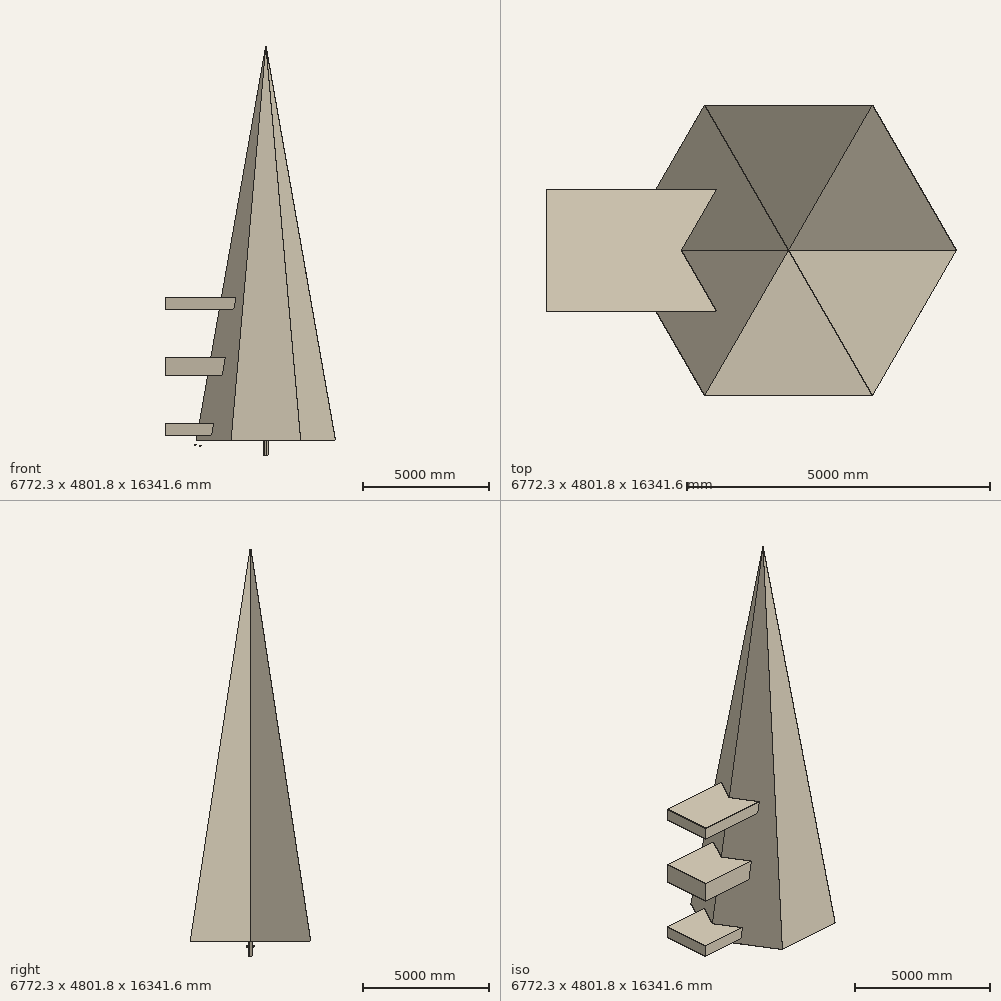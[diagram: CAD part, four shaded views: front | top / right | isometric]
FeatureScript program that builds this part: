
annotation { "Feature Type Name" : "Feature", "Feature Type Description" : "" }
export const myFeature = defineFeature(function(context is Context, id is Id, definition is map)
    precondition{}
    {
        {
            var Q0;
            Q0=qCreatedBy(makeId("Front.planeOp"),FACE);
            var sketch = newSketch(context, id + "F0", { "sketchPlane" : qUnion([Q0])});
            skLineSegment(sketch, "E0", {"start": v(-4000, 0) * mm, "end": v(4000, 0) * mm, "construction": true});
            skLineSegment(sketch, "E1", {"start": v(0, 7000) * mm, "end": v(0, -7000) * mm, "construction": true});
            skSolve(sketch);
        }
        {
            var Q0;
            Q0=qCreatedBy(makeId("Front.planeOp"),FACE);
            var sketch = newSketch(context, id + "F1", { "sketchPlane" : qUnion([Q0])});
            skLineSegment(sketch, "E2", {"start": v(0, 0) * mm, "end": v(0, 1682.58) * mm});
            skLineSegment(sketch, "E3.0", {"start": v(-2535.84, 600) * mm, "end": v(-2535.84, 612.7) * mm});
            skLineSegment(sketch, "E4", {"start": v(-3676.33, 0) * mm, "end": v(-2212.14, 0) * mm, "construction": true});
            skLineSegment(sketch, "E5.0", {"start": v(-2942.24, 600) * mm, "end": v(-2535.84, 600) * mm});
            skLineSegment(sketch, "E6.0", {"start": v(-2942.24, 612.7) * mm, "end": v(-2535.84, 612.7) * mm});
            skLineSegment(sketch, "E7.0", {"start": v(-2942.24, 600) * mm, "end": v(-2942.24, 612.7) * mm});
            skPoint(sketch, "E8.orphan", {"position": v(-2535.84, 0) * mm});
            skSolve(sketch);
        }
        {
            var Q0;
            Q0=makeQuery(id+"F1.imprint","IMPRINT",FACE,{"disambiguationData":[TD([[makeQuery(id+"F1.imprint","IMPRINT",EDGE,{"derivedFrom":sQuery(id+"F1.wireOp",EDGE,"E3.0")}),1.0]])]});
            extrude(context, id + "F2", {"entities" : qUnion([Q0]), "depth" : 304.8 * mm, "offsetDistance" : 25 * mm, "symmetric" : true});
        }
        {
            var Q0;
            Q0=makeQuery(id+"F2.opExtrude","CAP_FACE",FACE,{"disambiguationData":[OSD([sQuery(id+"F1.wireOp",EDGE,"E3.0"),sQuery(id+"F1.wireOp",EDGE,"E5.0"),sQuery(id+"F1.wireOp",EDGE,"E6.0"),sQuery(id+"F1.wireOp",EDGE,"E7.0")])],"isStart":false});
            var sketch = newSketch(context, id + "F3", { "sketchPlane" : qUnion([Q0])});
            skPoint(sketch, "E9.0", {"position": v(-2942.24, 606.35) * mm});
            skPoint(sketch, "E10.0", {"position": v(-2535.84, 606.35) * mm});
            skLineSegment(sketch, "E11", {"start": v(-2942.24, 606.35) * mm, "end": v(-2535.84, 606.35) * mm, "construction": true});
            skLineSegment(sketch, "E12", {"start": v(-2739.04, 606.35) * mm, "end": v(-2773.57, 410.51) * mm, "construction": true});
            skLineSegment(sketch, "E13", {"start": v(-2773.57, 410.51) * mm, "end": v(-2973.68, 445.8) * mm, "construction": true});
            skLineSegment(sketch, "E14.MirrorCS", {"start": v(-2773.57, 410.51) * mm, "end": v(-2573.46, 375.23) * mm, "construction": true});
            skLineSegment(sketch, "E15.0", {"start": v(-2772.47, 416.77) * mm, "end": v(-2972.58, 452.05) * mm});
            skLineSegment(sketch, "E16.0", {"start": v(-2772.47, 416.77) * mm, "end": v(-2572.35, 381.48) * mm});
            skLineSegment(sketch, "E17.0", {"start": v(-2774.67, 404.26) * mm, "end": v(-2974.79, 439.55) * mm});
            skLineSegment(sketch, "E18.0", {"start": v(-2774.67, 404.26) * mm, "end": v(-2574.56, 368.97) * mm});
            skLineSegment(sketch, "E19", {"start": v(-2972.58, 452.05) * mm, "end": v(-2974.79, 439.55) * mm});
            skLineSegment(sketch, "E20", {"start": v(-2572.35, 381.48) * mm, "end": v(-2574.56, 368.97) * mm});
            skSolve(sketch);
        }
        {
            var Q0;
            Q0=makeQuery(id+"F3.imprint","IMPRINT",FACE,{"disambiguationData":[TD([[makeQuery(id+"F3.imprint","IMPRINT",EDGE,{"derivedFrom":sQuery(id+"F3.wireOp",EDGE,"E15.0")}),1.0]])]});
            extrude(context, id + "F4", {"entities" : qUnion([Q0]), "oppositeDirection" : true, "depth" : 304.8 * mm, "offsetDistance" : 25 * mm});
        }
        {
            var Q0;
            Q0=qCreatedBy(makeId("Front.planeOp"),FACE);
            var sketch = newSketch(context, id + "F5", { "sketchPlane" : qUnion([Q0])});
            skLineSegment(sketch, "E21.0", {"start": v(-4000, 0) * mm, "end": v(4000, 0) * mm, "construction": true});
            skLineSegment(sketch, "E22.0", {"start": v(-4000, 6287.28) * mm, "end": v(0, 6287.28) * mm});
            skLineSegment(sketch, "E23.0", {"start": v(-4000, 6299.97) * mm, "end": v(0, 6299.97) * mm});
            skLineSegment(sketch, "E24", {"start": v(0, 6287.28) * mm, "end": v(0, 6299.97) * mm});
            skLineSegment(sketch, "E25", {"start": v(-4000, 6287.28) * mm, "end": v(-4000, 6299.97) * mm});
            skSolve(sketch);
        }
        {
            var Q0;
            Q0=makeQuery(id+"F4.opExtrude","SWEPT_FACE",FACE,{"disambiguationData":[OSD([sQuery(id+"F3.wireOp",EDGE,"E15.0"),sQuery(id+"F3.wireOp",EDGE,"E16.0")])]});
            var sketch = newSketch(context, id + "F6", { "sketchPlane" : qUnion([Q0])});
            skLineSegment(sketch, "E26", {"start": v(-3005.92, 0) * mm, "end": v(-2599.52, 0) * mm, "construction": true});
            skLineSegment(sketch, "E27", {"start": v(-2802.72, 152.4) * mm, "end": v(-2802.72, -152.4) * mm, "construction": true});
            skLineSegment(sketch, "E28.0", {"start": v(-2904.32, -76.2) * mm, "end": v(-2894.8, -76.2) * mm});
            skLineSegment(sketch, "E29.0", {"start": v(-2904.32, 76.2) * mm, "end": v(-2894.8, 76.2) * mm});
            skLineSegment(sketch, "E30.0", {"start": v(-2904.32, 76.2) * mm, "end": v(-2904.32, -76.2) * mm});
            skLineSegment(sketch, "E31.0", {"start": v(-2701.12, 76.2) * mm, "end": v(-2701.12, -76.2) * mm});
            skLineSegment(sketch, "E32.0", {"start": v(-2894.8, 76.2) * mm, "end": v(-2894.8, 4.76) * mm});
            skLineSegment(sketch, "E33.0", {"start": v(-2710.64, 76.2) * mm, "end": v(-2710.64, 4.76) * mm});
            skLineSegment(sketch, "E34.0", {"start": v(-2894.8, -4.76) * mm, "end": v(-2710.64, -4.76) * mm});
            skLineSegment(sketch, "E35.0", {"start": v(-2894.8, 4.76) * mm, "end": v(-2710.64, 4.76) * mm});
            skLineSegment(sketch, "E36.trimOffspring", {"start": v(-2710.64, 76.2) * mm, "end": v(-2701.12, 76.2) * mm});
            skLineSegment(sketch, "E37.trimOffspring", {"start": v(-2710.64, -76.2) * mm, "end": v(-2701.12, -76.2) * mm});
            skLineSegment(sketch, "E38.trimOffspring", {"start": v(-2894.8, -4.76) * mm, "end": v(-2894.8, -76.2) * mm});
            skLineSegment(sketch, "E39.trimOffspring", {"start": v(-2710.64, -4.76) * mm, "end": v(-2710.64, -76.2) * mm});
            skSolve(sketch);
        }
        {
            var Q0;
            Q0=makeQuery(id+"F5.imprint","IMPRINT",FACE,{"disambiguationData":[TD([[makeQuery(id+"F5.imprint","IMPRINT",EDGE,{"derivedFrom":sQuery(id+"F5.wireOp",EDGE,"E22.0")}),1.0]])]});
            extrude(context, id + "F7", {"entities" : qUnion([Q0]), "depth" : 2000 * mm, "offsetDistance" : 25 * mm, "symmetric" : true});
        }
        {
            var Q0;
            Q0=makeQuery(id+"F6.imprint","IMPRINT",FACE,{"disambiguationData":[TD([[makeQuery(id+"F6.imprint","IMPRINT",EDGE,{"derivedFrom":sQuery(id+"F6.wireOp",EDGE,"E28.0")}),1.0]])]});
            var Q1;
            Q1=makeQuery(id+"F7.opExtrude","SWEPT_FACE",FACE,{"disambiguationData":[OSD([sQuery(id+"F5.wireOp",EDGE,"E22.0")])]});
            extrude(context, id + "F8", {"entities" : qUnion([Q0]), "endBound" : BoundingType.UP_TO_SURFACE, "depth" : 25 * mm, "endBoundEntityFace" : qUnion([Q1]), "offsetDistance" : 25 * mm});
        }
        {
            var Q0;
            Q0=makeQuery(id+"F4.opExtrude","SWEPT_FACE",FACE,{"disambiguationData":[OSD([sQuery(id+"F3.wireOp",EDGE,"E15.0"),sQuery(id+"F3.wireOp",EDGE,"E16.0")])]});
            var sketch = newSketch(context, id + "F9", { "sketchPlane" : qUnion([Q0])});
            skLineSegment(sketch, "E40.0", {"start": v(-2904.32, 76.2) * mm, "end": v(-2904.32, -76.2) * mm, "construction": true});
            skLineSegment(sketch, "E41.0", {"start": v(-2836.58, 76.2) * mm, "end": v(-2836.58, -76.2) * mm, "construction": true});
            skLineSegment(sketch, "E42", {"start": v(-2836.58, 4.76) * mm, "end": v(-2686.48, 264.76) * mm});
            skLineSegment(sketch, "E43.0", {"start": v(-2827.42, 4.76) * mm, "end": v(-2677.31, 264.76) * mm});
            skLineSegment(sketch, "E44", {"start": v(-2827.42, 4.76) * mm, "end": v(-2836.58, 4.76) * mm});
            skLineSegment(sketch, "E45.0", {"start": v(-3005.92, 0) * mm, "end": v(-2599.52, 0) * mm, "construction": true});
            skLineSegment(sketch, "E46.MirrorCS", {"start": v(-2827.42, -4.76) * mm, "end": v(-2836.58, -4.76) * mm});
            skLineSegment(sketch, "E47.MirrorCS", {"start": v(-2827.42, -4.76) * mm, "end": v(-2677.31, -264.76) * mm});
            skLineSegment(sketch, "E48.MirrorCS", {"start": v(-2836.58, -4.76) * mm, "end": v(-2686.48, -264.76) * mm});
            skLineSegment(sketch, "E49", {"start": v(-2677.31, 264.76) * mm, "end": v(-2686.48, 264.76) * mm});
            skPoint(sketch, "E50.start.orphan", {"position": v(-2684.18, 268.73) * mm});
            skLineSegment(sketch, "E51", {"start": v(-2677.31, -264.76) * mm, "end": v(-2686.48, -264.76) * mm});
            skPoint(sketch, "E52.orphan", {"position": v(-2684.18, -268.73) * mm});
            skPoint(sketch, "E53.MirrorCS.end.orphan", {"position": v(-2677.31, -264.76) * mm});
            skSolve(sketch);
        }
        {
            var Q0;
            {var subQ0=sQuery(id+"F9.wireOp",EDGE,"E46.MirrorCS");Q0=makeQuery(id+"F9.imprint","IMPRINT",FACE,{"disambiguationData":[TD([[makeQuery(id+"F9.imprint","IMPRINT",EDGE,{"derivedFrom":subQ0}),1.0]])]});}
            var Q1;
            {var subQ0=sQuery(id+"F9.wireOp",EDGE,"E53.MirrorCS");Q1=makeQuery(id+"F9.imprint","IMPRINT",FACE,{"disambiguationData":[TD([[makeQuery(id+"F9.imprint","IMPRINT",EDGE,{"derivedFrom":subQ0}),1.0]])]});}
            var Q2;
            Q2=makeQuery(id+"F7.opExtrude","SWEPT_FACE",FACE,{"disambiguationData":[OSD([sQuery(id+"F5.wireOp",EDGE,"E22.0")])]});
            extrude(context, id + "F10", {"entities" : qUnion([Q0, Q1]), "endBound" : BoundingType.UP_TO_SURFACE, "depth" : 25 * mm, "endBoundEntityFace" : qUnion([Q2]), "offsetDistance" : 25 * mm});
        }
        {
            var Q0;
            {var subQ0=sQuery(id+"F9.wireOp",EDGE,"E50");Q0=makeQuery(id+"F9.imprint","IMPRINT",FACE,{"disambiguationData":[TD([[makeQuery(id+"F9.imprint","IMPRINT",EDGE,{"derivedFrom":subQ0}),-1.0]])]});}
            var Q1;
            {var subQ0=sQuery(id+"F9.wireOp",EDGE,"E44");Q1=makeQuery(id+"F9.imprint","IMPRINT",FACE,{"disambiguationData":[TD([[makeQuery(id+"F9.imprint","IMPRINT",EDGE,{"derivedFrom":subQ0}),-1.0]])]});}
            var Q2;
            Q2=makeQuery(id+"F7.opExtrude","SWEPT_FACE",FACE,{"disambiguationData":[OSD([sQuery(id+"F5.wireOp",EDGE,"E22.0")])]});
            extrude(context, id + "F11", {"entities" : qUnion([Q0, Q1]), "endBound" : BoundingType.UP_TO_SURFACE, "depth" : 25 * mm, "endBoundEntityFace" : qUnion([Q2]), "offsetDistance" : 25 * mm});
        }
        {
            var Q0;
            Q0=qCreatedBy(makeId("Front.planeOp"),FACE);
            var sketch = newSketch(context, id + "F12", { "sketchPlane" : qUnion([Q0])});
            skLineSegment(sketch, "E54.0", {"start": v(-4000, 0) * mm, "end": v(4000, 0) * mm, "construction": true});
            skLineSegment(sketch, "E55.0", {"start": v(-4000, 612.7) * mm, "end": v(4000, 612.7) * mm, "construction": true});
            skLineSegment(sketch, "E56.0", {"start": v(-4000, 809.66) * mm, "end": v(0, 809.66) * mm});
            skLineSegment(sketch, "E57.0", {"start": v(-4000, 1259.92) * mm, "end": v(0, 1259.92) * mm});
            skLineSegment(sketch, "E58.0", {"start": v(-4000, 3173.26) * mm, "end": v(0, 3173.26) * mm});
            skLineSegment(sketch, "E59.0", {"start": v(-4000, 3923.68) * mm, "end": v(0, 3923.68) * mm});
            skLineSegment(sketch, "E60.0", {"start": v(-4000, 5837.02) * mm, "end": v(0, 5837.02) * mm});
            skLineSegment(sketch, "E61.0", {"start": v(-4000, 6287.28) * mm, "end": v(0, 6287.28) * mm});
            skLineSegment(sketch, "E62.0", {"start": v(0, 7000) * mm, "end": v(0, -7000) * mm, "construction": true});
            skLineSegment(sketch, "E63", {"start": v(-4000, 809.66) * mm, "end": v(-4000, 1259.92) * mm});
            skLineSegment(sketch, "E64", {"start": v(0, 809.66) * mm, "end": v(0, 1259.92) * mm});
            skLineSegment(sketch, "E65", {"start": v(-4000, 3923.68) * mm, "end": v(-4000, 3173.26) * mm});
            skLineSegment(sketch, "E66", {"start": v(0, 3923.68) * mm, "end": v(0, 3173.26) * mm});
            skLineSegment(sketch, "E67", {"start": v(-4000, 6287.28) * mm, "end": v(-4000, 5837.02) * mm});
            skLineSegment(sketch, "E68", {"start": v(0, 6287.28) * mm, "end": v(0, 5837.02) * mm});
            skSolve(sketch);
        }
        {
            var Q0;
            Q0=makeQuery(id+"F12.imprint","IMPRINT",FACE,{"disambiguationData":[TD([[makeQuery(id+"F12.imprint","IMPRINT",EDGE,{"derivedFrom":sQuery(id+"F12.wireOp",EDGE,"E60.0")}),1.0]])]});
            var Q1;
            Q1=makeQuery(id+"F12.imprint","IMPRINT",FACE,{"disambiguationData":[TD([[makeQuery(id+"F12.imprint","IMPRINT",EDGE,{"derivedFrom":sQuery(id+"F12.wireOp",EDGE,"E58.0")}),1.0]])]});
            var Q2;
            Q2=makeQuery(id+"F12.imprint","IMPRINT",FACE,{"disambiguationData":[TD([[makeQuery(id+"F12.imprint","IMPRINT",EDGE,{"derivedFrom":sQuery(id+"F12.wireOp",EDGE,"E56.0")}),1.0]])]});
            extrude(context, id + "F13", {"entities" : qUnion([Q0, Q1, Q2]), "depth" : 2000 * mm, "offsetDistance" : 25 * mm, "symmetric" : true});
        }
        {
            var Q0;
            Q0=makeQuery(id+"F13.opExtrude","SWEPT_BODY",BODY,{"disambiguationData":[OSD([sQuery(id+"F12.wireOp",EDGE,"E56.0"),sQuery(id+"F12.wireOp",EDGE,"E57.0"),sQuery(id+"F12.wireOp",EDGE,"E63"),sQuery(id+"F12.wireOp",EDGE,"E64")])]});
            var Q1;
            Q1=makeQuery(id+"F10.opExtrude","SWEPT_BODY",BODY,{"disambiguationData":[OSD([sQuery(id+"F3.wireOp",EDGE,"E15.0"),sQuery(id+"F3.wireOp",EDGE,"E16.0"),sQuery(id+"F9.wireOp",EDGE,"E46.MirrorCS"),sQuery(id+"F9.wireOp",EDGE,"E47.MirrorCS"),sQuery(id+"F9.wireOp",EDGE,"E48.MirrorCS")])]});
            booleanBodies(context, id + "F14", {"operationType" : BooleanOperationType.INTERSECTION, "tools" : qUnion([Q0, Q1]), "keepTools" : true});
        }
        {
            var Q0;
            Q0=makeQuery(id+"F13.opExtrude","SWEPT_BODY",BODY,{"disambiguationData":[OSD([sQuery(id+"F12.wireOp",EDGE,"E58.0"),sQuery(id+"F12.wireOp",EDGE,"E59.0"),sQuery(id+"F12.wireOp",EDGE,"E65"),sQuery(id+"F12.wireOp",EDGE,"E66")])]});
            var Q1;
            Q1=makeQuery(id+"F10.opExtrude","SWEPT_BODY",BODY,{"disambiguationData":[OSD([sQuery(id+"F3.wireOp",EDGE,"E15.0"),sQuery(id+"F3.wireOp",EDGE,"E16.0"),sQuery(id+"F9.wireOp",EDGE,"E46.MirrorCS"),sQuery(id+"F9.wireOp",EDGE,"E47.MirrorCS"),sQuery(id+"F9.wireOp",EDGE,"E48.MirrorCS")])]});
            booleanBodies(context, id + "F15", {"operationType" : BooleanOperationType.INTERSECTION, "tools" : qUnion([Q0, Q1]), "keepTools" : true});
        }
        {
            var Q0;
            Q0=makeQuery(id+"F10.opExtrude","SWEPT_BODY",BODY,{"disambiguationData":[OSD([sQuery(id+"F3.wireOp",EDGE,"E15.0"),sQuery(id+"F3.wireOp",EDGE,"E16.0"),sQuery(id+"F9.wireOp",EDGE,"E46.MirrorCS"),sQuery(id+"F9.wireOp",EDGE,"E47.MirrorCS"),sQuery(id+"F9.wireOp",EDGE,"E48.MirrorCS")])]});
            var Q1;
            Q1=makeQuery(id+"F13.opExtrude","SWEPT_BODY",BODY,{"disambiguationData":[OSD([sQuery(id+"F12.wireOp",EDGE,"E60.0"),sQuery(id+"F12.wireOp",EDGE,"E61.0"),sQuery(id+"F12.wireOp",EDGE,"E67"),sQuery(id+"F12.wireOp",EDGE,"E68")])]});
            booleanBodies(context, id + "F16", {"operationType" : BooleanOperationType.INTERSECTION, "tools" : qUnion([Q0, Q1]), "keepTools" : true});
        }
        {
            var Q0;
            Q0=makeQuery(id+"F10.opExtrude","SWEPT_BODY",BODY,{"disambiguationData":[OSD([sQuery(id+"F3.wireOp",EDGE,"E15.0"),sQuery(id+"F3.wireOp",EDGE,"E16.0"),sQuery(id+"F9.wireOp",EDGE,"E46.MirrorCS"),sQuery(id+"F9.wireOp",EDGE,"E47.MirrorCS"),sQuery(id+"F9.wireOp",EDGE,"E48.MirrorCS")])]});
            deleteBodies(context, id + "F17", {"entities" : qUnion([Q0])});
        }
        {
            var Q0;
            Q0=makeQuery(id+"F13.opExtrude","SWEPT_BODY",BODY,{"disambiguationData":[OSD([sQuery(id+"F12.wireOp",EDGE,"E56.0"),sQuery(id+"F12.wireOp",EDGE,"E57.0"),sQuery(id+"F12.wireOp",EDGE,"E63"),sQuery(id+"F12.wireOp",EDGE,"E64")])]});
            var Q1;
            Q1=makeQuery(id+"F11.opExtrude","SWEPT_BODY",BODY,{"disambiguationData":[OSD([sQuery(id+"F3.wireOp",EDGE,"E15.0"),sQuery(id+"F3.wireOp",EDGE,"E16.0"),sQuery(id+"F9.wireOp",EDGE,"E42"),sQuery(id+"F9.wireOp",EDGE,"E43.0"),sQuery(id+"F9.wireOp",EDGE,"E44")])]});
            booleanBodies(context, id + "F18", {"operationType" : BooleanOperationType.INTERSECTION, "tools" : qUnion([Q0, Q1]), "keepTools" : true});
        }
        {
            var Q0;
            Q0=makeQuery(id+"F13.opExtrude","SWEPT_BODY",BODY,{"disambiguationData":[OSD([sQuery(id+"F12.wireOp",EDGE,"E58.0"),sQuery(id+"F12.wireOp",EDGE,"E59.0"),sQuery(id+"F12.wireOp",EDGE,"E65"),sQuery(id+"F12.wireOp",EDGE,"E66")])]});
            var Q1;
            Q1=makeQuery(id+"F11.opExtrude","SWEPT_BODY",BODY,{"disambiguationData":[OSD([sQuery(id+"F3.wireOp",EDGE,"E15.0"),sQuery(id+"F3.wireOp",EDGE,"E16.0"),sQuery(id+"F9.wireOp",EDGE,"E42"),sQuery(id+"F9.wireOp",EDGE,"E43.0"),sQuery(id+"F9.wireOp",EDGE,"E44")])]});
            booleanBodies(context, id + "F19", {"operationType" : BooleanOperationType.INTERSECTION, "tools" : qUnion([Q0, Q1]), "keepTools" : true});
        }
        {
            var Q0;
            Q0=makeQuery(id+"F13.opExtrude","SWEPT_BODY",BODY,{"disambiguationData":[OSD([sQuery(id+"F12.wireOp",EDGE,"E60.0"),sQuery(id+"F12.wireOp",EDGE,"E61.0"),sQuery(id+"F12.wireOp",EDGE,"E67"),sQuery(id+"F12.wireOp",EDGE,"E68")])]});
            var Q1;
            Q1=makeQuery(id+"F11.opExtrude","SWEPT_BODY",BODY,{"disambiguationData":[OSD([sQuery(id+"F3.wireOp",EDGE,"E15.0"),sQuery(id+"F3.wireOp",EDGE,"E16.0"),sQuery(id+"F9.wireOp",EDGE,"E42"),sQuery(id+"F9.wireOp",EDGE,"E43.0"),sQuery(id+"F9.wireOp",EDGE,"E44")])]});
            booleanBodies(context, id + "F20", {"operationType" : BooleanOperationType.INTERSECTION, "tools" : qUnion([Q0, Q1]), "keepTools" : true});
        }
        {
            var Q0;
            Q0=makeQuery(id+"F11.opExtrude","SWEPT_BODY",BODY,{"disambiguationData":[OSD([sQuery(id+"F3.wireOp",EDGE,"E15.0"),sQuery(id+"F3.wireOp",EDGE,"E16.0"),sQuery(id+"F9.wireOp",EDGE,"E42"),sQuery(id+"F9.wireOp",EDGE,"E43.0"),sQuery(id+"F9.wireOp",EDGE,"E44")])]});
            deleteBodies(context, id + "F21", {"entities" : qUnion([Q0])});
        }
        {
            var Q0;
            Q0=makeQuery(id+"F2.opExtrude","SWEPT_BODY",BODY,{"disambiguationData":[OSD([sQuery(id+"F1.wireOp",EDGE,"E3.0"),sQuery(id+"F1.wireOp",EDGE,"E5.0"),sQuery(id+"F1.wireOp",EDGE,"E6.0"),sQuery(id+"F1.wireOp",EDGE,"E7.0")])]});
            var Q1;
            Q1=makeQuery(id+"F8.opExtrude","SWEPT_BODY",BODY,{"disambiguationData":[OSD([sQuery(id+"F6.wireOp",EDGE,"E28.0"),sQuery(id+"F6.wireOp",EDGE,"E29.0"),sQuery(id+"F6.wireOp",EDGE,"E30.0"),sQuery(id+"F6.wireOp",EDGE,"E31.0"),sQuery(id+"F6.wireOp",EDGE,"E32.0"),sQuery(id+"F6.wireOp",EDGE,"E33.0"),sQuery(id+"F6.wireOp",EDGE,"E34.0"),sQuery(id+"F6.wireOp",EDGE,"E35.0"),sQuery(id+"F6.wireOp",EDGE,"E36.trimOffspring"),sQuery(id+"F6.wireOp",EDGE,"E37.trimOffspring"),sQuery(id+"F6.wireOp",EDGE,"E38.trimOffspring"),sQuery(id+"F6.wireOp",EDGE,"E39.trimOffspring")])]});
            booleanBodies(context, id + "F22", {"operationType" : BooleanOperationType.SUBTRACTION, "tools" : qUnion([Q0]), "targets" : qUnion([Q1]), "keepTools" : true});
        }
        {
            var Q0;
            Q0=makeQuery(id+"F22.opBoolean","SPLIT",BODY,{"disambiguationData":[OD(0.0)],"derivedFrom":makeQuery(id+"F8.opExtrude","SWEPT_BODY",BODY,{"disambiguationData":[OSD([sQuery(id+"F6.wireOp",EDGE,"E28.0"),sQuery(id+"F6.wireOp",EDGE,"E29.0"),sQuery(id+"F6.wireOp",EDGE,"E30.0"),sQuery(id+"F6.wireOp",EDGE,"E31.0"),sQuery(id+"F6.wireOp",EDGE,"E32.0"),sQuery(id+"F6.wireOp",EDGE,"E33.0"),sQuery(id+"F6.wireOp",EDGE,"E34.0"),sQuery(id+"F6.wireOp",EDGE,"E35.0"),sQuery(id+"F6.wireOp",EDGE,"E36.trimOffspring"),sQuery(id+"F6.wireOp",EDGE,"E37.trimOffspring"),sQuery(id+"F6.wireOp",EDGE,"E38.trimOffspring"),sQuery(id+"F6.wireOp",EDGE,"E39.trimOffspring")])]})});
            deleteBodies(context, id + "F23", {"entities" : qUnion([Q0])});
        }
        {
            var Q0;
            Q0=makeQuery(id+"F2.opExtrude","SWEPT_FACE",FACE,{"disambiguationData":[OSD([sQuery(id+"F1.wireOp",EDGE,"E6.0")])]});
            var sketch = newSketch(context, id + "F24", { "sketchPlane" : qUnion([Q0])});
            skLineSegment(sketch, "E69", {"start": v(-2942.24, 152.4) * mm, "end": v(-2942.24, -152.4) * mm, "construction": true});
            skLineSegment(sketch, "E70", {"start": v(-2942.24, -152.4) * mm, "end": v(-2535.84, -152.4) * mm, "construction": true});
            skLineSegment(sketch, "E71.0", {"start": v(-2891.44, 152.4) * mm, "end": v(-2891.44, -152.4) * mm, "construction": true});
            skLineSegment(sketch, "E72.0", {"start": v(-2942.24, -101.6) * mm, "end": v(-2535.84, -101.6) * mm, "construction": true});
            skLineSegment(sketch, "E73", {"start": v(-2942.24, 152.4) * mm, "end": v(-2535.84, 152.4) * mm, "construction": true});
            skLineSegment(sketch, "E74", {"start": v(-2535.84, 152.4) * mm, "end": v(-2535.84, -152.4) * mm, "construction": true});
            skLineSegment(sketch, "E75.0", {"start": v(-2942.24, 101.6) * mm, "end": v(-2535.84, 101.6) * mm, "construction": true});
            skLineSegment(sketch, "E76.0", {"start": v(-2586.64, 152.4) * mm, "end": v(-2586.64, -152.4) * mm, "construction": true});
            skCircle(sketch, "E77", {"center": v(-2891.44, 101.6) * mm, "radius": 10.32 * mm});
            skCircle(sketch, "E78", {"center": v(-2586.64, 101.6) * mm, "radius": 10.32 * mm});
            skCircle(sketch, "E79", {"center": v(-2891.44, -101.6) * mm, "radius": 10.32 * mm});
            skCircle(sketch, "E80", {"center": v(-2586.64, -101.6) * mm, "radius": 10.32 * mm});
            skSolve(sketch);
        }
        {
            var Q0;
            Q0=makeQuery(id+"F24.imprint","IMPRINT",FACE,{"disambiguationData":[TD([[makeQuery(id+"F24.imprint","IMPRINT",EDGE,{"derivedFrom":sQuery(id+"F24.wireOp",EDGE,"E79")}),1.0]])]});
            var Q1;
            Q1=makeQuery(id+"F24.imprint","IMPRINT",FACE,{"disambiguationData":[TD([[makeQuery(id+"F24.imprint","IMPRINT",EDGE,{"derivedFrom":sQuery(id+"F24.wireOp",EDGE,"E77")}),1.0]])]});
            var Q2;
            Q2=makeQuery(id+"F24.imprint","IMPRINT",FACE,{"disambiguationData":[TD([[makeQuery(id+"F24.imprint","IMPRINT",EDGE,{"derivedFrom":sQuery(id+"F24.wireOp",EDGE,"E78")}),1.0]])]});
            var Q3;
            Q3=makeQuery(id+"F24.imprint","IMPRINT",FACE,{"disambiguationData":[TD([[makeQuery(id+"F24.imprint","IMPRINT",EDGE,{"derivedFrom":sQuery(id+"F24.wireOp",EDGE,"E80")}),1.0]])]});
            extrude(context, id + "F25", {"entities" : qUnion([Q0, Q1, Q2, Q3]), "operationType" : NewBodyOperationType.REMOVE, "endBound" : BoundingType.THROUGH_ALL, "oppositeDirection" : true, "depth" : 25 * mm, "offsetDistance" : 25 * mm});
        }
        {
            var Q0;
            Q0=qCreatedBy(makeId("Top.planeOp"),FACE);
            var sketch = newSketch(context, id + "F26", { "sketchPlane" : qUnion([Q0])});
            skLineSegment(sketch, "E81", {"start": v(0, 0) * mm, "end": v(-100, 0) * mm, "construction": true});
            skLineSegment(sketch, "E82", {"start": v(0, 0) * mm, "end": v(-96.6, 25.88) * mm, "construction": true});
            skLineSegment(sketch, "E83", {"start": v(0, 0) * mm, "end": v(-70.71, -70.71) * mm, "construction": true});
            skCircle(sketch, "E84", {"center": v(0, 0) * mm, "radius": 100 * mm, "construction": true});
            skLineSegment(sketch, "E85", {"start": v(-96.6, 25.88) * mm, "end": v(-70.71, -70.71) * mm});
            skLineSegment(sketch, "E86.1.0", {"start": v(-70.71, -70.71) * mm, "end": v(25.88, -96.6) * mm});
            skLineSegment(sketch, "E86.2.0", {"start": v(25.88, -96.6) * mm, "end": v(96.6, -25.88) * mm});
            skLineSegment(sketch, "E86.3.0", {"start": v(96.6, -25.88) * mm, "end": v(70.71, 70.71) * mm});
            skLineSegment(sketch, "E86.4.0", {"start": v(70.71, 70.71) * mm, "end": v(-25.88, 96.6) * mm});
            skLineSegment(sketch, "E86.5.0", {"start": v(-25.88, 96.6) * mm, "end": v(-96.6, 25.88) * mm});
            skSolve(sketch);
        }
        {
            var Q0;
            Q0=makeQuery(id+"F26.imprint","IMPRINT",FACE,{"disambiguationData":[TD([[makeQuery(id+"F26.imprint","IMPRINT",EDGE,{"derivedFrom":sQuery(id+"F26.wireOp",EDGE,"E85")}),1.0]])]});
            extrude(context, id + "F27", {"entities" : qUnion([Q0]), "depth" : 7000 * mm, "offsetDistance" : 25 * mm});
        }
        {
            var Q0;
            Q0=qCreatedBy(makeId("Top.planeOp"),FACE);
            cPlane(context, id + "F28", {"entities" : qUnion([Q0]), "cplaneType" : CPlaneType.OFFSET, "offset" : 612.7 * mm, "width" : 150 * mm, "height" : 150 * mm});
        }
        {
            var Q0;
            Q0=qCreatedBy(id+"F28.planeOp",FACE);
            var sketch = newSketch(context, id + "F29", { "sketchPlane" : qUnion([Q0])});
            skLineSegment(sketch, "E87", {"start": v(0, 0) * mm, "end": v(-2772.3, 0) * mm, "construction": true});
            skCircle(sketch, "E88.cCircle", {"center": v(0, 0) * mm, "radius": 2772.3 * mm, "construction": true});
            skLineSegment(sketch, "E88.0", {"start": v(-2772.3, 0) * mm, "end": v(-1386.15, 2400.89) * mm});
            skLineSegment(sketch, "E88.1", {"start": v(-1386.15, 2400.89) * mm, "end": v(1386.15, 2400.89) * mm});
            skLineSegment(sketch, "E88.2", {"start": v(1386.15, 2400.89) * mm, "end": v(2772.3, 0) * mm});
            skLineSegment(sketch, "E88.3", {"start": v(2772.3, 0) * mm, "end": v(1386.15, -2400.89) * mm});
            skLineSegment(sketch, "E88.4", {"start": v(1386.15, -2400.89) * mm, "end": v(-1386.15, -2400.89) * mm});
            skLineSegment(sketch, "E88.5", {"start": v(-1386.15, -2400.89) * mm, "end": v(-2772.3, 0) * mm});
            skSolve(sketch);
        }
        {
            var Q0;
            Q0=qCreatedBy(id+"F28.planeOp",FACE);
            cPlane(context, id + "F30", {"entities" : qUnion([Q0]), "cplaneType" : CPlaneType.OFFSET, "offset" : 15728.89 * mm, "width" : 150 * mm, "height" : 150 * mm});
        }
        {
            var Q0;
            Q0=qCreatedBy(id+"F30.planeOp",FACE);
            var sketch = newSketch(context, id + "F31", { "sketchPlane" : qUnion([Q0])});
            skPoint(sketch, "E89", {"position": v(0, 0) * mm});
            skSolve(sketch);
        }
        {
            var Q1;
            Q1=sQuery(id+"F31.wireOp",VERTEX,"E89");
            var Q2;
            Q2=makeQuery(id+"F29.imprint","IMPRINT",FACE,{"disambiguationData":[TD([[makeQuery(id+"F29.imprint","IMPRINT",EDGE,{"derivedFrom":sQuery(id+"F29.wireOp",EDGE,"E88.0")}),-1.0]])]});
            loft(context, id + "F32", {"sheetProfilesArray" : [{ "sheetProfileEntities" : qUnion([Q1]) }, { "sheetProfileEntities" : qUnion([Q2]) }]});
        }
    });
